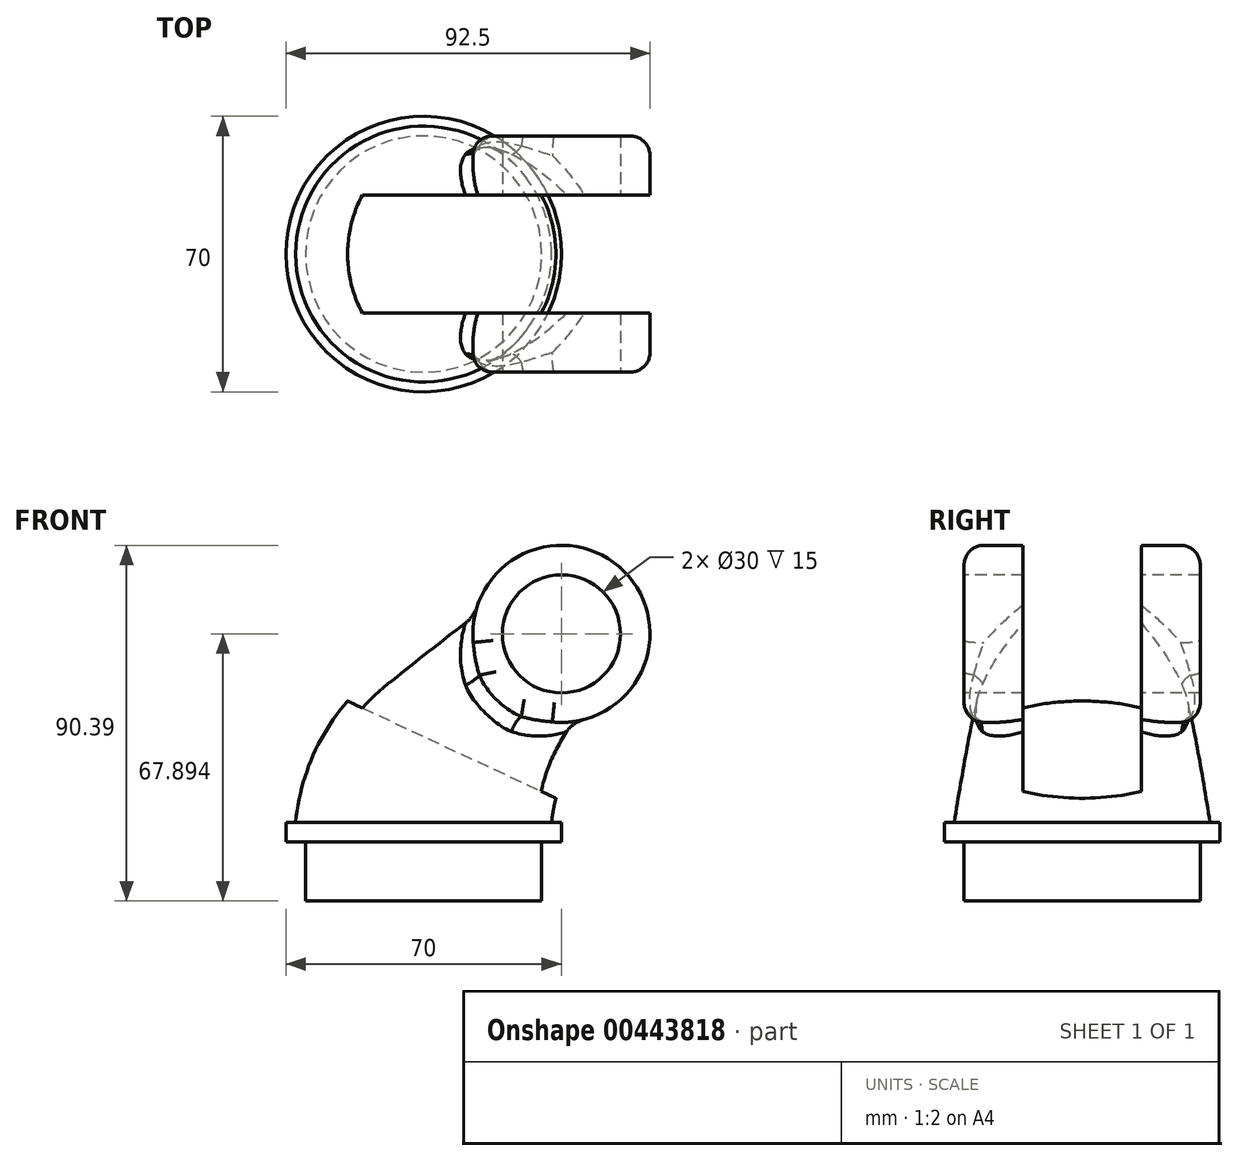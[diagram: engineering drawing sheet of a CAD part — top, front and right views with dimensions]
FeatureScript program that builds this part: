
annotation { "Feature Type Name" : "Feature", "Feature Type Description" : "" }
export const myFeature = defineFeature(function(context is Context, id is Id, definition is map)
    precondition{}
    {
        {
            var Q0;
            Q0=qCreatedBy(makeId("Top.planeOp"),FACE);
            var sketch = newSketch(context, id + "F0", { "sketchPlane" : qUnion([Q0])});
            skCircle(sketch, "E0", {"center": v(0, 0) * mm, "radius": 35 * mm});
            skSolve(sketch);
        }
        {
            var Q0;
            Q0 = qSketchRegion(id + "F0", true);
            extrude(context, id + "F1", {"entities" : qUnion([Q0]), "depth" : 5 * mm});
        }
        {
            var Q0;
            Q0=qCreatedBy(makeId("Front.planeOp"),FACE);
            var sketch = newSketch(context, id + "F2", { "sketchPlane" : qUnion([Q0])});
            skArc(sketch, "E1", {"start": v(17.6, 38.3) * mm, "mid": v(5.55, 23.37) * mm, "end": v(0, 5) * mm});
            skLineSegment(sketch, "E2", {"start": v(17.6, 38.3) * mm, "end": v(35, 52.9) * mm});
            skSolve(sketch);
        }
        {
            var Q0;
            Q0=sQuery(id+"F2.wireOp",VERTEX,"E2.end");
            var Q1;
            Q1=sQuery(id+"F2.wireOp",EDGE,"E2");
            cPlane(context, id + "F3", {"entities" : qUnion([Q0, Q1]), "cplaneType" : CPlaneType.LINE_POINT, "offset" : 25 * mm, "width" : 150 * mm, "height" : 150 * mm});
        }
        {
            var Q0;
            Q0=qCreatedBy(id+"F3.planeOp",FACE);
            var sketch = newSketch(context, id + "F4", { "sketchPlane" : qUnion([Q0])});
            skCircle(sketch, "E3", {"center": v(0, 18.02) * mm, "radius": 22.5 * mm});
            skSolve(sketch);
        }
        {
            var Q0;
            Q0=makeQuery(id+"F1.opExtrude","CAP_FACE",FACE,{"disambiguationData":[OSD([sQuery(id+"F0.wireOp",EDGE,"E0")])],"isStart":false});
            var sketch = newSketch(context, id + "F5", { "sketchPlane" : qUnion([Q0])});
            skCircle(sketch, "E4", {"center": v(0, 0) * mm, "radius": 32.5 * mm});
            skSolve(sketch);
        }
        {
            var Q0;
            Q0=qCreatedBy(makeId("Front.planeOp"),FACE);
            var sketch = newSketch(context, id + "F6", { "sketchPlane" : qUnion([Q0])});
            skArc(sketch, "E5", {"start": v(-13.25, 41.78) * mm, "mid": v(-26.5, 25.3) * mm, "end": v(-32.5, 5) * mm});
            skLineSegment(sketch, "E6", {"start": v(-13.25, 41.78) * mm, "end": v(20.54, 70.13) * mm});
            skSolve(sketch);
        }
        {
            var Q0;
            Q0=qCreatedBy(makeId("Front.planeOp"),FACE);
            var sketch = newSketch(context, id + "F7", { "sketchPlane" : qUnion([Q0])});
            skArc(sketch, "E7", {"start": v(48.46, 34.82) * mm, "mid": v(37.6, 21.45) * mm, "end": v(32.5, 5) * mm});
            skLineSegment(sketch, "E8", {"start": v(48.46, 34.82) * mm, "end": v(49.46, 35.66) * mm});
            skSolve(sketch);
        }
        {
            var Q1;
            Q1=makeQuery(id+"F4.imprint","IMPRINT",FACE,{"disambiguationData":[TD([[makeQuery(id+"F4.imprint","IMPRINT",EDGE,{"derivedFrom":sQuery(id+"F4.wireOp",EDGE,"E3")}),1.0]])]});
            var Q2;
            Q2=makeQuery(id+"F5.imprint","IMPRINT",FACE,{"disambiguationData":[TD([[makeQuery(id+"F5.imprint","IMPRINT",EDGE,{"derivedFrom":sQuery(id+"F5.wireOp",EDGE,"E4")}),1.0]])]});
            var Q3;
            Q3 = qConstructionFilter(qBodyType(qCreatedBy(id + "F6" ,EDGE), BodyType.WIRE), ConstructionObject.NO);
            var Q4;
            Q4 = qConstructionFilter(qBodyType(qCreatedBy(id + "F7" ,EDGE), BodyType.WIRE), ConstructionObject.NO);
            loft(context, id + "F8", {"operationType" : NewBodyOperationType.ADD, "addGuides" : true, "sheetProfilesArray" : [{ "sheetProfileEntities" : qUnion([Q1]) }, { "sheetProfileEntities" : qUnion([Q2]) }], "guidesArray" : [{ "guideEntities" : qUnion([Q3]), "guideDerivativeType" : LoftGuideDerivativeType.DEFAULT, "guideDerivativeMagnitude" : 1 }, { "guideEntities" : qUnion([Q4]), "guideDerivativeType" : LoftGuideDerivativeType.DEFAULT, "guideDerivativeMagnitude" : 1 }]});
        }
        {
            var Q0;
            Q0=qCreatedBy(makeId("Front.planeOp"),FACE);
            var sketch = newSketch(context, id + "F9", { "sketchPlane" : qUnion([Q0])});
            skCircle(sketch, "E9", {"center": v(35, 52.9) * mm, "radius": 22.5 * mm});
            skSolve(sketch);
        }
        {
            var Q0;
            Q0 = qSketchRegion(id + "F9", true);
            extrude(context, id + "F10", {"entities" : qUnion([Q0]), "operationType" : NewBodyOperationType.ADD, "endBound" : BoundingType.SYMMETRIC, "depth" : 60 * mm});
        }
        {
            var Q0;
            Q0=makeQuery(id+"F10.boolean.opBoolean","INTERSECT",EDGE,{"disambiguationData":[OD(0.0)],"derivedFrom":[makeQuery(id+"F8.opLoft","SWEPT_FACE",FACE,{"disambiguationData":[OSD([sQuery(id+"F4.wireOp",EDGE,"E3"),sQuery(id+"F5.wireOp",EDGE,"E4"),sQuery(id+"F6.wireOp",VERTEX,"E6.start"),sQuery(id+"F6.wireOp",EDGE,"E5"),sQuery(id+"F6.wireOp",EDGE,"E6"),sQuery(id+"F7.wireOp",VERTEX,"E8.start"),sQuery(id+"F7.wireOp",EDGE,"E7"),sQuery(id+"F7.wireOp",EDGE,"E8")])]}),makeQuery(id+"F10.opExtrude","SWEPT_FACE",FACE,{"disambiguationData":[OSD([sQuery(id+"F9.wireOp",EDGE,"E9")])]})]});
            var Q1;
            Q1=makeQuery(id+"F10.boolean.opBoolean","INTERSECT",EDGE,{"disambiguationData":[OD(1.0)],"derivedFrom":[makeQuery(id+"F8.opLoft","SWEPT_FACE",FACE,{"disambiguationData":[OSD([sQuery(id+"F4.wireOp",EDGE,"E3"),sQuery(id+"F5.wireOp",EDGE,"E4"),sQuery(id+"F6.wireOp",VERTEX,"E6.start"),sQuery(id+"F6.wireOp",EDGE,"E5"),sQuery(id+"F6.wireOp",EDGE,"E6"),sQuery(id+"F7.wireOp",VERTEX,"E8.start"),sQuery(id+"F7.wireOp",EDGE,"E7"),sQuery(id+"F7.wireOp",EDGE,"E8")])]}),makeQuery(id+"F10.opExtrude","SWEPT_FACE",FACE,{"disambiguationData":[OSD([sQuery(id+"F9.wireOp",EDGE,"E9")])]})]});
            fillet(context, id + "F11", {"entities" : qUnion([Q0, Q1]), "radius" : 5 * mm, "tangentPropagation" : true, "allowEdgeOverflow" : false});
        }
        {
            var Q0;
            Q0=makeQuery(id+"F10.opExtrude","CAP_EDGE",EDGE,{"disambiguationData":[OSD([sQuery(id+"F9.wireOp",EDGE,"E9")])],"isStart":false});
            var Q1;
            Q1=makeQuery(id+"F10.opExtrude","CAP_EDGE",EDGE,{"disambiguationData":[OSD([sQuery(id+"F9.wireOp",EDGE,"E9")])],"isStart":true});
            fillet(context, id + "F12", {"entities" : qUnion([Q0, Q1]), "radius" : 5 * mm, "tangentPropagation" : true, "allowEdgeOverflow" : false});
        }
        {
            var Q0;
            Q0=makeQuery(id+"F10.opExtrude","CAP_FACE",FACE,{"disambiguationData":[OSD([sQuery(id+"F9.wireOp",EDGE,"E9")])],"isStart":false});
            var sketch = newSketch(context, id + "F13", { "sketchPlane" : qUnion([Q0])});
            skCircle(sketch, "E10", {"center": v(35, 52.9) * mm, "radius": 15 * mm});
            skSolve(sketch);
        }
        {
            var Q0;
            Q0 = qSketchRegion(id + "F13", true);
            extrude(context, id + "F14", {"entities" : qUnion([Q0]), "operationType" : NewBodyOperationType.REMOVE, "endBound" : BoundingType.THROUGH_ALL, "oppositeDirection" : true, "depth" : 25 * mm});
        }
        {
            var Q0;
            Q0=qCreatedBy(makeId("Front.planeOp"),FACE);
            var sketch = newSketch(context, id + "F15", { "sketchPlane" : qUnion([Q0])});
            skLineSegment(sketch, "E11", {"start": v(-104.18, 75.4) * mm, "end": v(57.5, 0) * mm});
            skLineSegment(sketch, "E12", {"start": v(57.5, 75.4) * mm, "end": v(57.5, 0) * mm});
            skLineSegment(sketch, "E13", {"start": v(-104.18, 75.4) * mm, "end": v(57.5, 75.4) * mm});
            skSolve(sketch);
        }
        {
            var Q0;
            Q0=makeQuery(id+"F15.imprint","IMPRINT",FACE,{"disambiguationData":[TD([[makeQuery(id+"F15.imprint","IMPRINT",EDGE,{"derivedFrom":sQuery(id+"F15.wireOp",EDGE,"E11")}),1.0]])]});
            extrude(context, id + "F16", {"entities" : qUnion([Q0]), "operationType" : NewBodyOperationType.REMOVE, "endBound" : BoundingType.SYMMETRIC, "oppositeDirection" : true, "depth" : 30 * mm});
        }
        {
            var Q0;
            Q0=qCreatedBy(makeId("Front.planeOp"),FACE);
            var sketch = newSketch(context, id + "F17", { "sketchPlane" : qUnion([Q0])});
            skLineSegment(sketch, "E14.bottom", {"start": v(0, 0) * mm, "end": v(-30, 0) * mm});
            skLineSegment(sketch, "E14.top", {"start": v(0, -15) * mm, "end": v(-30, -15) * mm});
            skLineSegment(sketch, "E14.left", {"start": v(0, 0) * mm, "end": v(0, -15) * mm});
            skLineSegment(sketch, "E14.right", {"start": v(-30, 0) * mm, "end": v(-30, -15) * mm});
            skSolve(sketch);
        }
        {
            var Q0;
            Q0 = qSketchRegion(id + "F17", true);
            var Q1;
            Q1=sQuery(id+"F17.wireOp",EDGE,"E14.left");
            revolve(context, id + "F18", {"operationType" : NewBodyOperationType.ADD, "entities" : qUnion([Q0]), "axis" : qUnion([Q1]), "revolveType" : RevolveType.FULL});
        }
    });
